# Revit family: Legrand Benelux Snap on Columns
name_source: partatom
category: Installations électriques
units: mm (PartAtom-declared; Revit-internal decimal feet)

## family parameters
Basée sur le plan de construction = Non
Conserver l'orientation des annotations = Non
Cote de connecteur circulaire = Utiliser le diamètre
Couper avec des vides une fois chargée = Oui
Partagée = Non
Point de calcul de pièce = Non
Toujours verticalement = Oui
Type d'élément = Normal

## types (15) — shared parameters
Fabricant = LEGRAND
Standard = Snap-on-ON
zero-valued in all types: Elévation par défaut

## per-type parameters (varying)
| type | 1 CPT | 2 CPT | 4 CPT | Description | Finishing | Finishing kit for telescopic pole | H1 | HC | Largeur | Longueur | Main Material | Matériau couvercle | Matériaux corps | Modèle | Number of compartments | Séparateur |
| Column 1 cpt CV45 2,67M White | Oui | Non | Non | Column direct clipping 1 compartment 2,670m White | White | Finishing kit for telescopic pole : White CV perche for Column | 2700 mm | 2660 mm  [stored 8.72703 ft] | 75 mm | 82 mm | Aluminum | Legrand - Plastique blanc | Legrand - Aluminium blanc | LG-653010 | 1 compartment | 35 mm  [stored 0.114829 ft] |
| Column 1 cpt CV45 2,67M Alu | Oui | Non | Non | Column direct clipping 1 compartment 2,67m Aluminium | Aluminum | Finishing kit for telescopic pole : Grey CV  perche for Column | 2700 mm | 2660 mm  [stored 8.72703 ft] | 75 mm | 82 mm | Aluminum | Legrand - Plastique gris | Legrand - Aluminium gris | LG-653011 | 1 compartment | 35 mm  [stored 0.114829 ft] |
| Column 1 cpt CV45 2,67M Black | Oui | Non | Non | Column direct clipping 1 compartment 2,67m Black | Black | Finishing kit for telescopic pole : Black CV  perche for Column | 2700 mm | 2660 mm  [stored 8.72703 ft] | 75 mm | 82 mm | Aluminum | Legrand - Plastique noir | Legrand - Aluminium noir | LG-653012 | 1 compartment | 35 mm  [stored 0.114829 ft] |
| Column 1 cpt CV45 3,92M White | Oui | Non | Non | Column direct clipping 1 compartment 3,92m White | White | Finishing kit for telescopic pole : White CV perche for Column | 3900 mm | 3860 mm | 75 mm | 82 mm | Aluminum | Legrand - Plastique blanc | Legrand - Aluminium blanc | LG-653013 | 1 compartment | 35 mm  [stored 0.114829 ft] |
| Column 1 cpt CV45 3,92M Alu | Oui | Non | Non | Column direct clipping 1 compartment 3,92m Aluminium | Aluminum | Finishing kit for telescopic pole : Grey CV  perche for Column | 3900 mm | 3860 mm | 75 mm | 82 mm | Aluminum | Legrand - Plastique gris | Legrand - Aluminium gris | LG-653014 | 1 compartment | 35 mm  [stored 0.114829 ft] |
| Column 1 cpt CV45 3,92M Black | Oui | Non | Non | Column direct clipping 1 compartment 3,92m Black | Black | Finishing kit for telescopic pole : Black CV  perche for Column | 3900 mm | 3860 mm | 75 mm | 82 mm | Aluminum | Legrand - Plastique noir | Legrand - Aluminium noir | LG-653015 | 1 compartment | 35 mm  [stored 0.114829 ft] |
| Column 2 cpts 45 2,67M White | Non | Oui | Non | Column direct clipping 2 compartments 2,67m White | White | Finishing kit for telescopic pole : White CV perche for Column | 2700 mm | 2660 mm  [stored 8.72703 ft] | 75 mm | 125 mm  [stored 0.410105 ft] | Plastic | Legrand - Plastique blanc | Legrand - Plastique blanc | LG-653030 | 2 compartments | 35 mm  [stored 0.114829 ft] |
| Column 2 cpts CV45 2,67M Alu | Non | Oui | Non | Column direct clipping 2 compartments 2,67m Aluminium | Aluminum | Finishing kit for telescopic pole : Grey CV  perche for Column | 2700 mm | 2660 mm  [stored 8.72703 ft] | 75 mm | 125 mm  [stored 0.410105 ft] | Aluminum | Legrand - Plastique gris | Legrand - Aluminium gris | LG-653031 | 2 compartments | 35 mm  [stored 0.114829 ft] |
| Column 2 cpts CV45 2,67M Black | Non | Oui | Non | Column direct clipping 2 compartments 2,67m Black | Black | Finishing kit for telescopic pole : Black CV  perche for Column | 2700 mm | 2660 mm  [stored 8.72703 ft] | 75 mm | 125 mm  [stored 0.410105 ft] | Aluminum | Legrand - Plastique noir | Legrand - Aluminium noir | LG-653032 | 2 compartments | 35 mm  [stored 0.114829 ft] |
| Column 2 cpts CV45 3,92M White | Non | Oui | Non | Column direct clipping 2 compartments 3,92m White | White | Finishing kit for telescopic pole : White CV perche for Column | 3900 mm | 3860 mm | 75 mm | 125 mm  [stored 0.410105 ft] | Plastic | Legrand - Plastique blanc | Legrand - Plastique blanc | LG-653033 | 2 compartments | 35 mm  [stored 0.114829 ft] |
| Column 2 cpts CV45 3,92M Alu | Non | Oui | Non | Column direct clipping 2 compartments 3,92m Aluminium | Aluminum | Finishing kit for telescopic pole : Grey CV  perche for Column | 3900 mm | 3860 mm | 75 mm | 125 mm  [stored 0.410105 ft] | Aluminum | Legrand - Plastique gris | Legrand - Aluminium gris | LG-653034 | 2 compartments | 35 mm  [stored 0.114829 ft] |
| Column 2 cpts CV45 3,92M Black | Non | Oui | Non | Column direct clipping 2 compartments 3,92m Black | Black | Finishing kit for telescopic pole : Black CV  perche for Column | 3900 mm | 3860 mm | 75 mm | 125 mm  [stored 0.410105 ft] | Aluminum | Legrand - Plastique noir | Legrand - Aluminium noir | LG-653035 | 2 compartments | 35 mm  [stored 0.114829 ft] |
| Column 4 cpts CV45 2,67M White | Non | Non | Oui | Column direct clipping 4 compartments 2,670m White | White | Finishing kit for telescopic pole : White CV perche for Column | 680 mm  [stored 2.23097 ft] | 640 mm  [stored 2.09974 ft] | 125 mm  [stored 0.410105 ft] | 125 mm  [stored 0.410105 ft] | Aluminum | Legrand - Plastique blanc | Legrand - Aluminium blanc | LG-653050 | 4 compartments | 125 mm  [stored 0.410105 ft] |
| Column 4 cpts CV45 2,67M Alu | Non | Non | Oui | Column direct clipping 4 compartments 2,670m Aluminium | Aluminum | Finishing kit for telescopic pole : Grey CV  perche for Column | 680 mm  [stored 2.23097 ft] | 640 mm  [stored 2.09974 ft] | 125 mm  [stored 0.410105 ft] | 125 mm  [stored 0.410105 ft] | Aluminum | Legrand - Aluminium gris | Legrand - Aluminium gris | LG-653051 | 4 compartments | 125 mm  [stored 0.410105 ft] |
| Column 4 cpts CV45 2,67M Black | Non | Non | Oui | Column direct clipping 4 compartments 2,670m Black | Black | Finishing kit for telescopic pole : Black CV  perche for Column | 680 mm  [stored 2.23097 ft] | 640 mm  [stored 2.09974 ft] | 125 mm  [stored 0.410105 ft] | 125 mm  [stored 0.410105 ft] | Aluminum | Legrand - Plastique noir | Legrand - Aluminium noir | LG-653052 | 4 compartments | 125 mm  [stored 0.410105 ft] |

note: [stored X ft] marks values corroborated as IEEE doubles in the binary element streams (Revit-internal decimal feet)
